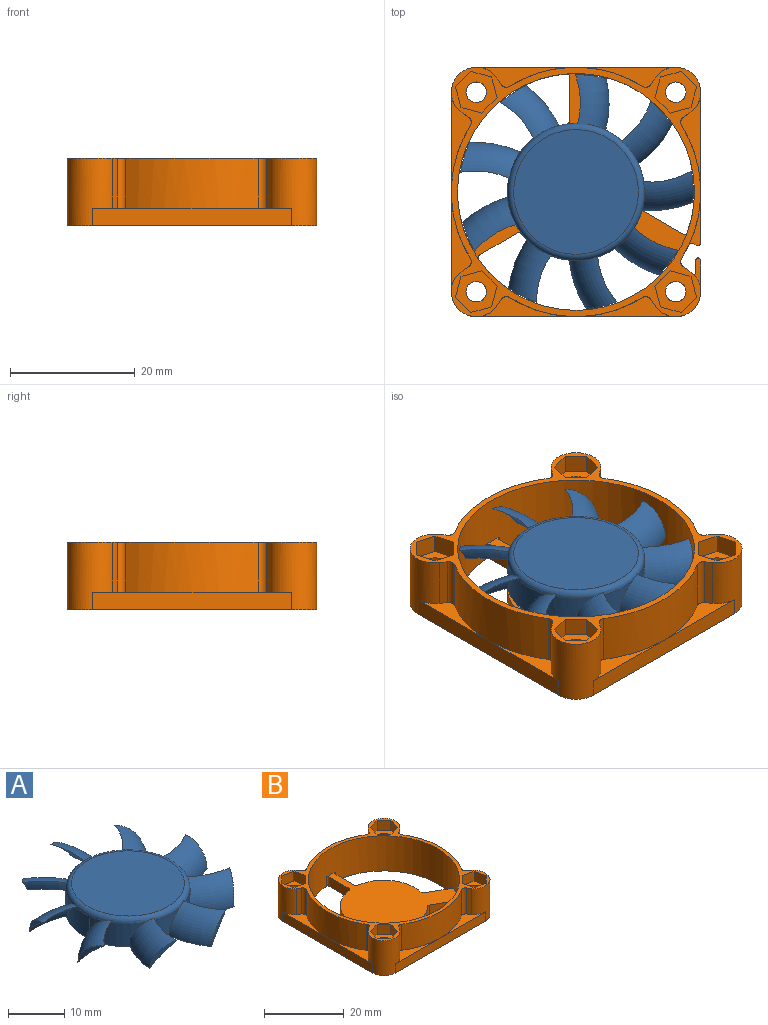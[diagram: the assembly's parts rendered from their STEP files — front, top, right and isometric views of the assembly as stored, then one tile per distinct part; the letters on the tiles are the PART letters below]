
ASSEMBLY  parts=2 mates=1
PART A: 32 faces, bbox 42.3x42.5x6 mm
  f0: cylinder r=11mm len=22mm, axis (0,0,-1), area 307.6mm2, adj f1,f3,f4,f5,f6,f8,f9,f11
  f1: cylinder r=11mm len=4.52mm, axis (0,0,-1), area 3.9mm2, adj f0,f4,f11
  f2: plane 20x20mm, normal (0,0,1), area 314.2mm2, adj f4
  f3: plane 22x22mm, normal (0,0,-1), area 380.1mm2, adj f0
  f4: torus R=10mm, axis (0,0,1), area 102.2mm2, adj f0,f1,f2,f5,f6,f8,f9,f11
  f5: torus R=12.73mm, axis (0,0,-1), area 60.3mm2, adj f0,f4,f6,f7
  f6: torus R=5.4mm, axis (0,0,-1), area 55.4mm2, adj f0,f4,f5,f7
  f7: cylinder r=18.8mm len=4.97mm, axis (0,0,1), area 4.5mm2, adj f5,f6
  f8: torus R=12.73mm, axis (0,0,-1), area 60.3mm2, adj f0,f4,f9,f10
  f9: torus R=5.4mm, axis (0,0,-1), area 55.4mm2, adj f0,f4,f8,f10
  f10: cylinder r=18.8mm len=4.97mm, axis (0,0,1), area 4.5mm2, adj f8,f9
  f11: torus R=12.73mm, axis (0,0,-1), area 60.3mm2, adj f0,f1,f4,f12,f13
  f12: torus R=5.4mm, axis (0,0,-1), area 55.4mm2, adj f0,f4,f11,f13
  f13: cylinder r=18.8mm len=4.97mm, axis (0,0,1), area 4.5mm2, adj f11,f12
  f14: torus R=12.73mm, axis (0,0,-1), area 60.3mm2, adj f0,f4,f15,f16
  f15: torus R=5.4mm, axis (0,0,-1), area 55.4mm2, adj f0,f4,f14,f16
  f16: cylinder r=18.8mm len=4.97mm, axis (0,0,1), area 4.5mm2, adj f14,f15
  f17: torus R=12.73mm, axis (0,0,-1), area 60.3mm2, adj f0,f4,f18,f19
  f18: torus R=5.4mm, axis (0,0,-1), area 55.4mm2, adj f0,f4,f17,f19
  f19: cylinder r=18.8mm len=4.97mm, axis (0,0,1), area 4.5mm2, adj f17,f18
  f20: torus R=12.73mm, axis (0,0,-1), area 60.3mm2, adj f0,f4,f21,f22
  f21: torus R=5.4mm, axis (0,0,-1), area 55.4mm2, adj f0,f4,f20,f22
  f22: cylinder r=18.8mm len=4.99mm, axis (0,0,1), area 4.5mm2, adj f20,f21
  f23: torus R=12.73mm, axis (0,0,-1), area 60.3mm2, adj f0,f4,f24,f25
  f24: torus R=5.4mm, axis (0,0,-1), area 55.4mm2, adj f0,f4,f23,f25
  f25: cylinder r=18.8mm len=4.97mm, axis (0,0,1), area 4.5mm2, adj f23,f24
  f26: torus R=12.73mm, axis (0,0,-1), area 60.3mm2, adj f0,f4,f27,f28
  f27: torus R=5.4mm, axis (0,0,-1), area 55.4mm2, adj f0,f4,f26,f28
  f28: cylinder r=18.8mm len=5mm, axis (0,0,1), area 4.5mm2, adj f26,f27
  f29: torus R=12.73mm, axis (0,0,-1), area 60.3mm2, adj f0,f4,f30,f31
  f30: torus R=5.4mm, axis (0,0,-1), area 55.4mm2, adj f0,f4,f29,f31
  f31: cylinder r=18.8mm len=4.97mm, axis (0,0,1), area 4.5mm2, adj f29,f30
PART B: 115 faces, bbox 40x40x10.8 mm
  f0: plane 10.28x5.94mm, normal (0.5,0.87,0), area 21.3mm2, adj f19,f33,f35,f80,f81,f82
  f1: plane 2.8x1.78mm, normal (-1,0,0), area 5mm2, adj f8,f33,f81,f97
  f2: plane 16x3.21mm, normal (0,0,1), area 18mm2, adj f26,f27,f56,f57,f100
  f3: plane 16x3.21mm, normal (0,0,1), area 18mm2, adj f25,f26,f65,f69,f106
  f4: plane 16x3.21mm, normal (0,0,1), area 18mm2, adj f21,f22,f34,f60,f102
  f5: plane 16x3.21mm, normal (0,0,1), area 18mm2, adj f23,f24,f62,f63,f104
  f6: plane 16x3.21mm, normal (0,0,1), area 18mm2, adj f27,f28,f57,f58,f101
  f7: plane 35.04x31.24mm, normal (0,0,1), area 457.1mm2, adj f12,f13,f14,f15,f16,f17,f18,f30
  f8: plane 5.45x1.07mm, normal (0,0,1), area 3mm2, adj f1,f28,f29,f81,f96,f97
  f9: plane 16x3.21mm, normal (0,0,1), area 18mm2, adj f22,f23,f61,f62,f103
  f10: plane 8.58x1.89mm, normal (0,0,1), area 5.1mm2, adj f20,f21,f34,f76,f89
  f11: plane 16x3.21mm, normal (0,0,1), area 18mm2, adj f24,f25,f64,f65,f105
  f12: plane 7.04x2.8mm, normal (1,0,0), area 19.7mm2, adj f7,f33,f87,f92
  f13: cylinder r=19mm len=38mm, axis (0,0,1), area 1253.2mm2, adj f7,f33,f71,f83,f84,f85,f86,f87
  f14: plane 6.22x3.59mm, normal (0.5,0.87,0), area 20.1mm2, adj f7,f33,f88,f95
  f15: plane 6.09x3.52mm, normal (0.5,-0.87,0), area 19.7mm2, adj f7,f33,f84,f90
  f16: cylinder r=11mm len=16.31mm, axis (0,0,1), area 51.7mm2, adj f7,f33,f90,f94
  f17: plane 6.09x3.52mm, normal (-0.5,0.87,0), area 19.7mm2, adj f7,f33,f85,f91
  f18: plane 7.04x2.8mm, normal (-1,0,0), area 19.7mm2, adj f7,f33,f86,f93
  f19: cylinder r=11mm len=3.9mm, axis (0,0,1), area 8mm2, adj f0,f20,f33,f35,f77
  f20: plane 8.8x5.08mm, normal (-0.5,-0.87,0), area 14.2mm2, adj f10,f19,f33,f76,f77,f78,f89
  f21: plane 24.08x2.8mm, normal (1,0,0), area 67.4mm2, adj f4,f10,f22,f33,f89
  f22: cylinder r=4mm len=10.8mm, axis (0,0,1), area 129.5mm2, adj f4,f9,f21,f23,f33,f60,f61,f71
  f23: plane 32x2.8mm, normal (0,1,0), area 89.6mm2, adj f5,f9,f22,f24,f33
  f24: cylinder r=4mm len=10.8mm, axis (0,0,1), area 129.5mm2, adj f5,f11,f23,f25,f33,f63,f64,f71
  f25: plane 32x2.8mm, normal (-1,0,0), area 89.6mm2, adj f3,f11,f24,f26,f33
  f26: cylinder r=4mm len=10.8mm, axis (0,0,1), area 129.5mm2, adj f2,f3,f25,f27,f33,f56,f69,f71
  f27: plane 32x2.8mm, normal (0,-1,0), area 89.6mm2, adj f2,f6,f26,f28,f33
  f28: cylinder r=4mm len=10.8mm, axis (0,0,1), area 129.9mm2, adj f6,f8,f27,f29,f33,f58,f59,f71
  f29: plane 4.96x2.8mm, normal (1,0,0), area 13.9mm2, adj f8,f28,f33,f96
  f30: plane 6.22x3.59mm, normal (-0.5,-0.87,0), area 20.1mm2, adj f7,f33,f83,f94
  f31: cylinder r=11mm len=15.12mm, axis (0,0,1), area 56.4mm2, adj f7,f33,f91,f93
  f32: cylinder r=11mm len=13.49mm, axis (0,0,1), area 51.7mm2, adj f7,f33,f92,f95
  f33: plane 40x40mm, normal (0,0,-1), area 793.4mm2, adj f0,f1,f12,f13,f14,f15,f16,f17
  f34: cylinder r=20mm len=21.25mm, axis (0,0,1), area 180.4mm2, adj f4,f10,f71,f76,f79,f98,f102
  f35: plane 9.49x8.4mm, normal (0,0,-1), area 34.2mm2, adj f0,f19,f77,f79,f80
  f36: plane 3.35x3mm, normal (-0.26,-0.97,0), area 10.4mm2, adj f37,f70,f71,f75
  f37: plane 3.35x3mm, normal (-0.97,-0.26,0), area 10.4mm2, adj f36,f38,f71,f75
  f38: plane 3x2.45mm, normal (-0.71,0.71,0), area 10.4mm2, adj f37,f39,f71,f75
  f39: plane 3.35x3mm, normal (0.26,0.97,0), area 10.4mm2, adj f38,f40,f71,f75
  f40: plane 3.35x3mm, normal (0.97,0.26,0), area 10.4mm2, adj f39,f70,f71,f75
  f41: plane 3x2.45mm, normal (-0.71,0.71,0), area 10.4mm2, adj f42,f66,f71,f73
  f42: plane 3.35x3mm, normal (0.26,0.97,0), area 10.4mm2, adj f41,f43,f71,f73
  f43: plane 3.35x3mm, normal (0.97,0.26,0), area 10.4mm2, adj f42,f44,f71,f73
  f44: plane 3x2.45mm, normal (0.71,-0.71,0), area 10.4mm2, adj f43,f45,f71,f73
  f45: plane 3.35x3mm, normal (-0.26,-0.97,0), area 10.4mm2, adj f44,f66,f71,f73
  f46: plane 3.35x3mm, normal (-0.97,0.26,0), area 10.4mm2, adj f47,f67,f71,f72
  f47: plane 3.35x3mm, normal (-0.26,0.97,0), area 10.4mm2, adj f46,f48,f71,f72
  f48: plane 3x2.45mm, normal (0.71,0.71,0), area 10.4mm2, adj f47,f49,f71,f72
  f49: plane 3.35x3mm, normal (0.97,-0.26,0), area 10.4mm2, adj f48,f50,f71,f72
  f50: plane 3.35x3mm, normal (0.26,-0.97,0), area 10.4mm2, adj f49,f67,f71,f72
  f51: plane 3x2.45mm, normal (-0.71,-0.71,0), area 10.4mm2, adj f52,f68,f71,f74
  f52: plane 3.35x3mm, normal (-0.97,0.26,0), area 10.4mm2, adj f51,f53,f71,f74
  f53: plane 3.35x3mm, normal (-0.26,0.97,0), area 10.4mm2, adj f52,f54,f71,f74
  f54: plane 3x2.45mm, normal (0.71,0.71,0), area 10.4mm2, adj f53,f55,f71,f74
  f55: plane 3.35x3mm, normal (0.97,-0.26,0), area 10.4mm2, adj f54,f68,f71,f74
  f56: plane 8x1.06mm, normal (0.82,-0.57,0), area 10.4mm2, adj f2,f26,f71,f100
  f57: cylinder r=20mm len=21.25mm, axis (0,0,-1), area 179.2mm2, adj f2,f6,f71,f100,f101
  f58: plane 8x1.06mm, normal (-0.82,-0.57,0), area 10.4mm2, adj f6,f28,f71,f101
  f59: plane 8.5x1.06mm, normal (0.57,0.82,0), area 11mm2, adj f28,f71,f80,f98
  f60: plane 8x1.06mm, normal (0.57,-0.82,0), area 10.4mm2, adj f4,f22,f71,f102
  f61: plane 8x1.06mm, normal (-0.82,0.57,0), area 10.4mm2, adj f9,f22,f71,f103
  f62: cylinder r=20mm len=21.25mm, axis (0,0,-1), area 179.2mm2, adj f5,f9,f71,f103,f104
  f63: plane 8x1.06mm, normal (0.82,0.57,0), area 10.4mm2, adj f5,f24,f71,f104
  f64: plane 8x1.06mm, normal (-0.57,-0.82,0), area 10.4mm2, adj f11,f24,f71,f105
  f65: cylinder r=20mm len=21.25mm, axis (0,0,-1), area 179.2mm2, adj f3,f11,f71,f105,f106
  f66: plane 3.35x3mm, normal (-0.97,-0.26,0), area 10.4mm2, adj f41,f45,f71,f73
  f67: plane 3x2.45mm, normal (-0.71,-0.71,0), area 10.4mm2, adj f46,f50,f71,f72
  f68: plane 3.35x3mm, normal (0.26,-0.97,0), area 10.4mm2, adj f51,f55,f71,f74
  f69: plane 8x1.06mm, normal (-0.57,0.82,0), area 10.4mm2, adj f3,f26,f71,f106
  f70: plane 3x2.45mm, normal (0.71,-0.71,0), area 10.4mm2, adj f36,f40,f71,f75
  f71: plane 40x40mm, normal (0,0,1), area 183.3mm2, adj f13,f22,f24,f26,f28,f34,f36,f37
  f72: plane 6.69x6.69mm, normal (0,0,1), area 22.6mm2, adj f46,f47,f48,f49,f50,f67,f111
  f73: plane 6.69x6.69mm, normal (0,0,1), area 22.6mm2, adj f41,f42,f43,f44,f45,f66,f109
  f74: plane 6.69x6.69mm, normal (0,0,1), area 22.6mm2, adj f51,f52,f53,f54,f55,f68,f107
  f75: plane 6.69x6.69mm, normal (0,0,1), area 22.6mm2, adj f36,f37,f38,f39,f40,f70,f113
  f76: cylinder r=0.5mm len=0.7mm, axis (0,0,1), area 0.4mm2, adj f10,f20,f34,f78
  f77: cylinder r=0.5mm len=7.74mm, axis (0.87,-0.5,0), area 6.8mm2, adj f19,f20,f35,f78
  f78: bspline ~1.22x1.19mm, area 0.9mm2, adj f20,f76,f77,f79
  f79: torus R=19.5mm, axis (0,0,1), area 2.5mm2, adj f34,f35,f78,f99
  f80: cylinder r=0.5mm len=2.57mm, axis (0.82,-0.57,0), area 1.5mm2, adj f0,f35,f59,f82,f99
  f81: cylinder r=0.5mm len=2.8mm, axis (0,0,-1), area 2.6mm2, adj f0,f1,f8,f28,f33,f82
  f82: torus R=3.5mm, axis (0,0,1), area 0.4mm2, adj f0,f28,f80,f81
  f83: cylinder r=0.5mm len=2.8mm, axis (0,0,1), area 2.4mm2, adj f7,f13,f30,f33
  f84: cylinder r=0.5mm len=2.8mm, axis (0,0,1), area 2.3mm2, adj f7,f13,f15,f33
  f85: cylinder r=0.5mm len=2.8mm, axis (0,0,1), area 2.3mm2, adj f7,f13,f17,f33
  f86: cylinder r=0.5mm len=2.8mm, axis (0,0,1), area 2.3mm2, adj f7,f13,f18,f33
  f87: cylinder r=0.5mm len=2.8mm, axis (0,0,1), area 2.3mm2, adj f7,f12,f13,f33
  f88: cylinder r=0.5mm len=2.8mm, axis (0,0,1), area 2.4mm2, adj f7,f13,f14,f33
  f89: cylinder r=0.5mm len=2.8mm, axis (0,0,-1), area 2.9mm2, adj f10,f20,f21,f33
  f90: cylinder r=0.5mm len=2.8mm, axis (0,0,1), area 2mm2, adj f7,f15,f16,f33
  f91: cylinder r=0.5mm len=2.8mm, axis (0,0,1), area 2mm2, adj f7,f17,f31,f33
  f92: cylinder r=0.5mm len=2.8mm, axis (0,0,1), area 2mm2, adj f7,f12,f32,f33
  f93: cylinder r=0.5mm len=2.8mm, axis (0,0,1), area 2mm2, adj f7,f18,f31,f33
  f94: cylinder r=0.5mm len=2.8mm, axis (0,0,1), area 1.8mm2, adj f7,f16,f30,f33
  f95: cylinder r=0.5mm len=2.8mm, axis (0,0,1), area 1.8mm2, adj f7,f14,f32,f33
  f96: cylinder r=0.5mm len=2.8mm, axis (0,0,1), area 1.9mm2, adj f8,f29,f33,f97
  f97: cylinder r=0.5mm len=2.8mm, axis (0,0,1), area 1.9mm2, adj f1,f8,f33,f96
  f98: cylinder r=1mm len=8.5mm, axis (0,0,1), area 12.9mm2, adj f34,f59,f71,f99
  f99: bspline ~1.5x1.35mm, area 0.5mm2, adj f79,f80,f98
  f100: cylinder r=1mm len=8mm, axis (0,0,-1), area 12.2mm2, adj f2,f56,f57,f71
  f101: cylinder r=1mm len=8mm, axis (0,0,-1), area 12.2mm2, adj f6,f57,f58,f71
  f102: cylinder r=1mm len=8mm, axis (0,0,1), area 12.2mm2, adj f4,f34,f60,f71
  f103: cylinder r=1mm len=8mm, axis (0,0,-1), area 12.2mm2, adj f9,f61,f62,f71
  f104: cylinder r=1mm len=8mm, axis (0,0,-1), area 12.2mm2, adj f5,f62,f63,f71
  f105: cylinder r=1mm len=8mm, axis (0,0,-1), area 12.2mm2, adj f11,f64,f65,f71
  f106: cylinder r=1mm len=8mm, axis (0,0,-1), area 12.2mm2, adj f3,f65,f69,f71
  f107: cylinder r=1.65mm len=7.2mm, axis (0,0,-1), area 74.6mm2, adj f74,f108
  f108: cone r=1.65mm half-angle=45deg, axis (0,0,-1), area 10.4mm2, adj f33,f107
  f109: cylinder r=1.65mm len=7.2mm, axis (0,0,-1), area 74.6mm2, adj f73,f110
  f110: cone r=1.65mm half-angle=45deg, axis (0,0,-1), area 10.4mm2, adj f33,f109
  f111: cylinder r=1.65mm len=7.2mm, axis (0,0,-1), area 74.6mm2, adj f72,f112
  f112: cone r=1.65mm half-angle=45deg, axis (0,0,-1), area 10.4mm2, adj f33,f111
  f113: cylinder r=1.65mm len=7.2mm, axis (0,0,-1), area 74.6mm2, adj f75,f114
  f114: cone r=1.65mm half-angle=45deg, axis (0,0,-1), area 10.4mm2, adj f33,f113
PLACE A rot(axis=(0,0,-1),81.8deg) t=(0,0,0)mm
PLACE B at identity fixed
MATE revolute A.f0 <-> B.f13  axis (0,0,-1) through (0,0,0)mm
